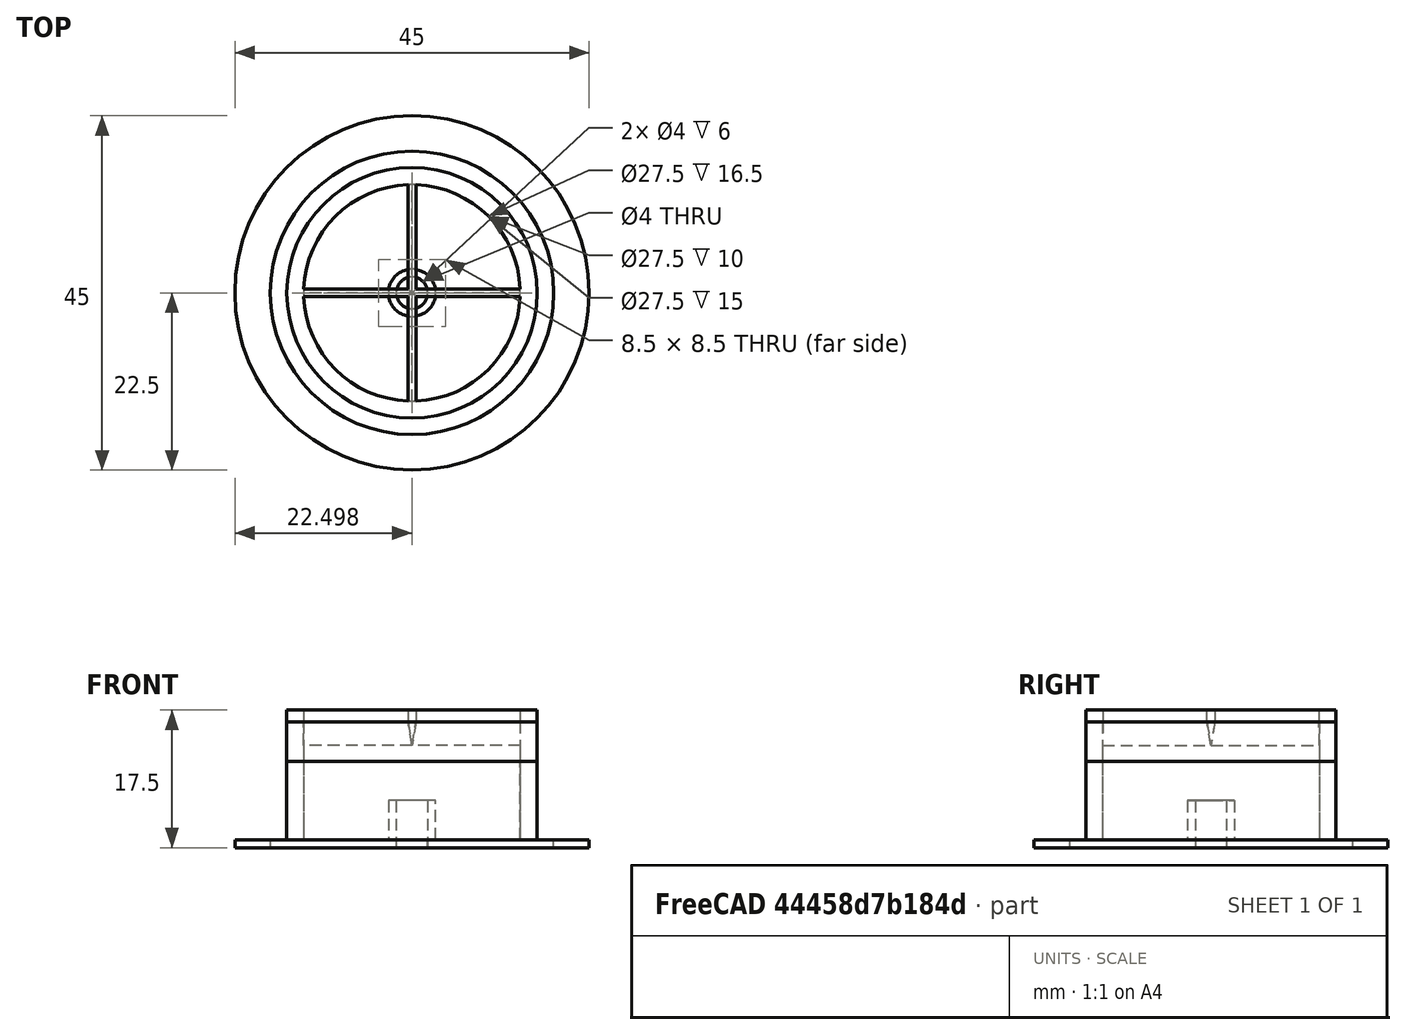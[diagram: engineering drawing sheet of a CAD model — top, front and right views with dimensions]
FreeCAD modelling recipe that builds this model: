
FCSTD DOCUMENT  (FreeCAD 0.20R29177 +426 (Git))
Label: Collimator
License: All rights reserved
LicenseURL: http://en.wikipedia.org/wiki/All_rights_reserved
objects: Part::Extrusion×15, Part::Part2DObjectPython×12, Part::MultiFuse×8, Part::Feature×5, Part::Cut×5, Part::Refine×5
note: 50 computed .brp shape members not serialized (recipe doc carries the construction recipe); baked Part::Feature solids carry a one-line shape summary decoded from their .brp

FEATURE [Part::Feature] Fusion001_solid  label="Fusion001 (Solid)"
  Placement = pos=(55.4975,-3.4e-15,0) rot=(0,0,1;0rad)
  shape: bbox 34 x 34 x 11 mm, 20 faces (baked)
FEATURE [Part::Part2DObjectPython] Circle  # Draft 2D object (typed FeaturePython)
  Area = 593.957
  FirstAngle = 0
  LastAngle = 0
  MakeFace = true
  Placement = pos=(55.4975,-3.4e-15,10) rot=(0,0,1;0rad)
  Radius = 13.75
FEATURE [Part::Part2DObjectPython] Circle001  # Draft 2D object (typed FeaturePython)
  Area = 794.226
  FirstAngle = 0
  LastAngle = 0
  MakeFace = true
  Placement = pos=(55.4975,-3.6e-15,10) rot=(0,0,1;0rad)
  Radius = 15.9
FEATURE [Part::Extrusion] Extrusion
  Base = -> Circle001
  Dir = (0,0,-10)
  DirMode = 0
  FaceMakerClass = Part::FaceMakerBullseye
  LengthFwd = 0
  LengthRev = 0
  Solid = true
  Symmetric = false
FEATURE [Part::Extrusion] Extrusion001
  Base = -> Circle
  Dir = (0,0,-10)
  DirMode = 0
  FaceMakerClass = Part::FaceMakerBullseye
  LengthFwd = 0
  LengthRev = 0
  Solid = true
  Symmetric = false
FEATURE [Part::Cut] Cut
  Base = -> Extrusion
  Tool = -> Extrusion001
FEATURE [Part::MultiFuse] Fusion
  Shapes = -> [Fusion001_solid,Cut]
FEATURE [Part::Part2DObjectPython] Circle002  # Draft 2D object (typed FeaturePython)
  Area = 779.311
  FirstAngle = 0
  LastAngle = 0
  MakeFace = true
  Placement = pos=(55.4975,-3.5e-15,-1) rot=(1,0,0;3.14159rad)
  Radius = 15.75
FEATURE [Part::Part2DObjectPython] Circle003  # Draft 2D object (typed FeaturePython)
  Area = 1017.88
  FirstAngle = 0
  LastAngle = 0
  MakeFace = true
  Placement = pos=(55.4975,1.1e-15,-1) rot=(1,0,0;3.14159rad)
  Radius = 18
FEATURE [Part::Extrusion] Extrusion002
  Base = -> Circle002
  Dir = (0,0,1)
  DirMode = 0
  FaceMakerClass = Part::FaceMakerBullseye
  LengthFwd = 0
  LengthRev = 0
  Solid = true
  Symmetric = false
FEATURE [Part::Extrusion] Extrusion003
  Base = -> Circle003
  Dir = (0,0,1)
  DirMode = 0
  FaceMakerClass = Part::FaceMakerBullseye
  LengthFwd = 0
  LengthRev = 0
  Solid = true
  Symmetric = false
FEATURE [Part::Cut] Cut001
  Base = -> Extrusion003
  Tool = -> Extrusion002
FEATURE [Part::MultiFuse] Fusion001
  Shapes = -> [Cut001,Fusion]
FEATURE [Part::Feature] Fusion001_solid001  label="Fusion001 (Solid)001"
  shape: bbox 36 x 36 x 11 mm, 25 faces (baked)
FEATURE [Part::Part2DObjectPython] Circle004  # Draft 2D object (typed FeaturePython)
  Area = 12.5664
  FirstAngle = 0
  LastAngle = 0
  MakeFace = true
  Placement = pos=(55.4975,-3.5e-15,0) rot=(0,0,1;0rad)
  Radius = 2
FEATURE [Part::Part2DObjectPython] Circle005  # Draft 2D object (typed FeaturePython)
  Area = 28.2743
  FirstAngle = 0
  LastAngle = 0
  MakeFace = true
  Placement = pos=(55.4975,-3.6e-15,0) rot=(0,0,1;0rad)
  Radius = 3
FEATURE [Part::Extrusion] Extrusion004
  Base = -> Circle004
  Dir = (0,0,5)
  DirMode = 0
  FaceMakerClass = Part::FaceMakerBullseye
  LengthFwd = 0
  LengthRev = 0
  Solid = true
  Symmetric = false
FEATURE [Part::Extrusion] Extrusion005
  Base = -> Circle005
  Dir = (0,0,5)
  DirMode = 0
  FaceMakerClass = Part::FaceMakerBullseye
  LengthFwd = 0
  LengthRev = 0
  Solid = true
  Symmetric = false
FEATURE [Part::Cut] Cut002
  Base = -> Extrusion005
  Tool = -> Extrusion004
FEATURE [Part::MultiFuse] Fusion002
  Shapes = -> [Fusion001_solid001,Cut002]
FEATURE [Part::Refine] Fusion002001
  Source = -> Fusion002
FEATURE [Part::Feature] Face
  shape: bbox 31.8 x 31.8 x 2e-07 mm, 1 faces, 0 solids (baked)
FEATURE [Part::Extrusion] Extrusion006
  Base = -> Face
  Dir = (0,0,5)
  DirMode = 0
  FaceMakerClass = Part::FaceMakerBullseye
  LengthFwd = 0
  LengthRev = 0
  Solid = true
  Symmetric = false
FEATURE [Part::MultiFuse] Fusion002002
  Shapes = -> [Fusion002001,Extrusion006]
FEATURE [Part::Refine] Fusion002002001
  Source = -> Fusion002002
FEATURE [Part::Part2DObjectPython] Rectangle  # Draft 2D object (typed FeaturePython)
  Area = 27.9693
  ChamferSize = 0
  Columns = 1
  FilletRadius = 0
  Height = 27.9693
  Length = 1
  MakeFace = true
  Placement = pos=(54.9975,-13.9847,15) rot=(0,0,1;0rad)
  Rows = 1
FEATURE [Part::Part2DObjectPython] Rectangle001  # Draft 2D object (typed FeaturePython)
  Area = 27.9406
  ChamferSize = 0
  Columns = 1
  FilletRadius = 0
  Height = 1
  Length = 27.9406
  MakeFace = true
  Placement = pos=(41.5272,-0.5,15) rot=(0,0,1;0rad)
  Rows = 1
FEATURE [Part::Extrusion] Extrusion007
  Base = -> Rectangle001
  Dir = (0,0,3)
  DirMode = 0
  FaceMakerClass = Part::FaceMakerBullseye
  LengthFwd = 0
  LengthRev = 0
  Solid = true
  Symmetric = false
FEATURE [Part::Extrusion] Extrusion008
  Base = -> Rectangle
  Dir = (0,0,3)
  DirMode = 0
  FaceMakerClass = Part::FaceMakerBullseye
  LengthFwd = 0
  LengthRev = 0
  Solid = true
  Symmetric = false
FEATURE [Part::Part2DObjectPython] Wire  # Draft 2D object (typed FeaturePython)
  Area = 1.5
  ChamferSize = 0
  Closed = true
  End = (69.4679,-0.5,15)
  FilletRadius = 0
  Length = 7.08276
  MakeFace = true
  Placement = pos=(69.4679,0.5,15) rot=(0.57735,0.57735,0.57735;2.0944rad)
  Points = (3) [(0,0,0),(-0.5,-3,0),(-1,0,0)]
  Start = (69.4679,0.5,15)
  Subdivisions = 0
FEATURE [Part::Extrusion] Extrusion009
  Base = -> Wire
  Dir = (-27.9406,0,0)
  DirMode = 0
  FaceMakerClass = Part::FaceMakerBullseye
  LengthFwd = 0
  LengthRev = 0
  Solid = true
  Symmetric = false
FEATURE [Part::Part2DObjectPython] Wire001  # Draft 2D object (typed FeaturePython)
  Area = 1.5
  ChamferSize = 0
  Closed = true
  End = (54.9975,-13.9847,15)
  FilletRadius = 0
  Length = 7.08276
  MakeFace = true
  Placement = pos=(55.9975,-13.9847,15) rot=(1,0,0;1.5708rad)
  Points = (3) [(0,0,0),(-0.5,-3,0),(-1,0,0)]
  Start = (55.9975,-13.9847,15)
  Subdivisions = 0
FEATURE [Part::Extrusion] Extrusion010
  Base = -> Wire001
  Dir = (-4e-16,27.9693,-6.2e-15)
  DirMode = 0
  FaceMakerClass = Part::FaceMakerBullseye
  LengthFwd = 0
  LengthRev = 0
  Solid = true
  Symmetric = false
FEATURE [Part::MultiFuse] Fusion002002002
  Shapes = -> [Extrusion010,Extrusion008,Extrusion007,Extrusion009]
FEATURE [Part::Refine] Fusion002002002001
  Source = -> Fusion002002002
FEATURE [Part::Feature] Face001
  shape: bbox 27.94 x 27.97 x 2e-07 mm, 1 faces, 0 solids (baked)
FEATURE [Part::Extrusion] Extrusion011
  Base = -> Face001
  Dir = (0,0,-1.5)
  DirMode = 0
  FaceMakerClass = Part::FaceMakerBullseye
  LengthFwd = 0
  LengthRev = 0
  Solid = true
  Symmetric = false
FEATURE [Part::Cut] Cut003
  Base = -> Fusion002002002001
  Tool = -> Extrusion011
FEATURE [Part::Feature] Face002
  Placement = pos=(0,0,5) rot=(0,0,1;0rad)
  shape: bbox 31.8 x 31.8 x 2e-07 mm, 1 faces, 0 solids (baked)
FEATURE [Part::Extrusion] Extrusion012
  Base = -> Face002
  Dir = (0,0,1.5)
  DirMode = 0
  FaceMakerClass = Part::FaceMakerBullseye
  LengthFwd = 0
  LengthRev = 0
  Solid = true
  Symmetric = false
FEATURE [Part::MultiFuse] Fusion002002002002
  Shapes = -> [Fusion002002,Extrusion012]
FEATURE [Part::MultiFuse] Fusion002002002003
  Shapes = -> [Fusion002002002002,Cut003]
FEATURE [Part::Refine] Fusion002002002003001
  Source = -> Fusion002002002003
FEATURE [Part::Part2DObjectPython] Circle006  # Draft 2D object (typed FeaturePython)
  Area = 1590.43
  FirstAngle = 0
  LastAngle = 0
  MakeFace = true
  Placement = pos=(55.4975,2e-15,-1) rot=(1,0,0;3.14159rad)
  Radius = 22.5
FEATURE [Part::Part2DObjectPython] Circle007  # Draft 2D object (typed FeaturePython)
  Area = 907.92
  FirstAngle = 0
  LastAngle = 0
  MakeFace = true
  Placement = pos=(55.4975,2e-15,-1) rot=(1,0,0;3.14159rad)
  Radius = 17
FEATURE [Part::Extrusion] Extrusion013
  Base = -> Circle007
  Dir = (0,0,1)
  DirMode = 0
  FaceMakerClass = Part::FaceMakerBullseye
  LengthFwd = 0
  LengthRev = 0
  Solid = true
  Symmetric = false
FEATURE [Part::Extrusion] Extrusion014
  Base = -> Circle006
  Dir = (0,0,1)
  DirMode = 0
  FaceMakerClass = Part::FaceMakerBullseye
  LengthFwd = 0
  LengthRev = 0
  Solid = true
  Symmetric = false
FEATURE [Part::Cut] Cut004
  Base = -> Extrusion014
  Tool = -> Extrusion013
FEATURE [Part::MultiFuse] Fusion002002002003002
  Shapes = -> [Fusion002002001,Cut004]
FEATURE [Part::Refine] Fusion002002002003002001
  Source = -> Fusion002002002003002
